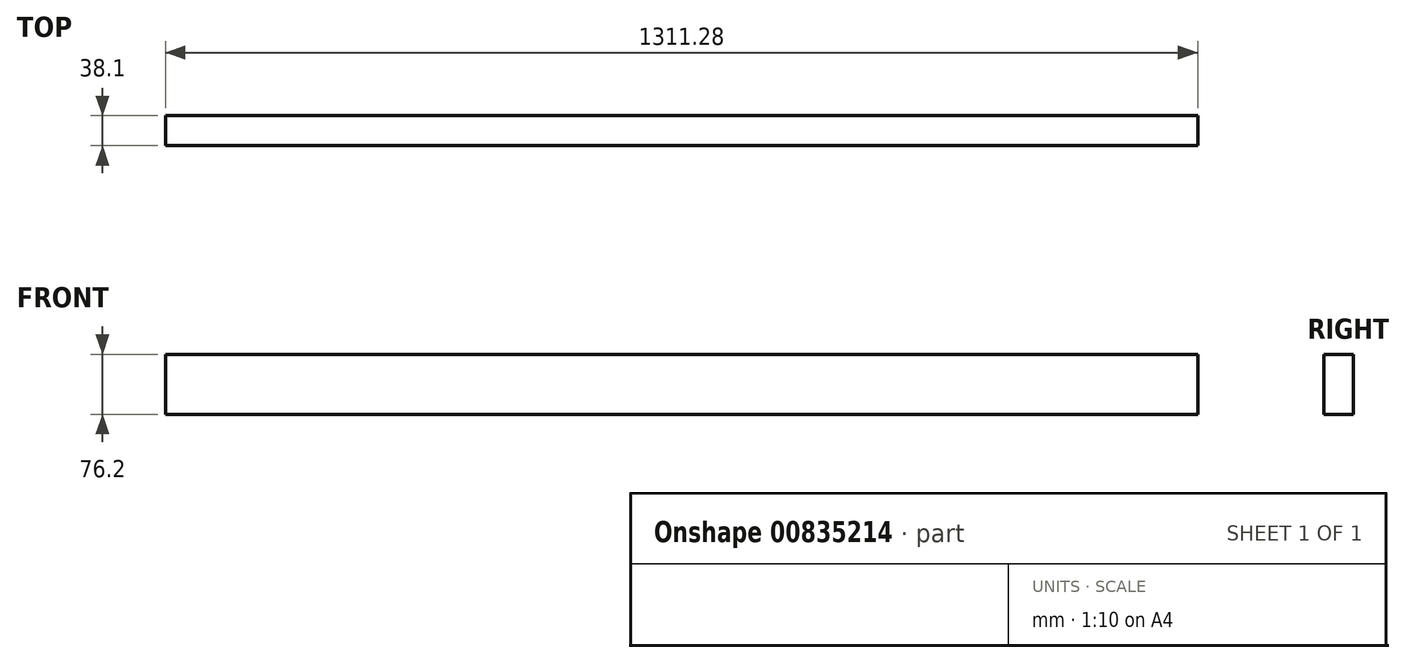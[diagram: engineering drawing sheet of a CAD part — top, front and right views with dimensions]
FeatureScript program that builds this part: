
annotation { "Feature Type Name" : "Feature", "Feature Type Description" : "" }
export const myFeature = defineFeature(function(context is Context, id is Id, definition is map)
    precondition{}
    {
        {
            var Q0;
            Q0=qCreatedBy(makeId("Right.planeOp"),FACE);
            var sketch = newSketch(context, id + "F0", { "sketchPlane" : qUnion([Q0])});
            skLineSegment(sketch, "E0.bottom", {"start": v(19.05, 38.1) * mm, "end": v(-19.05, 38.1) * mm});
            skLineSegment(sketch, "E0.top", {"start": v(19.05, -38.1) * mm, "end": v(-19.05, -38.1) * mm});
            skLineSegment(sketch, "E0.left", {"start": v(19.05, 38.1) * mm, "end": v(19.05, -38.1) * mm});
            skLineSegment(sketch, "E0.right", {"start": v(-19.05, 38.1) * mm, "end": v(-19.05, -38.1) * mm});
            skPoint(sketch, "E0.middle", {"position": v(0, 0) * mm});
            skSolve(sketch);
        }
        {
            var Q0;
            Q0 = qSketchRegion(id + "F0", true);
            extrude(context, id + "F1", {"entities" : qUnion([Q0]), "endBound" : BoundingType.SYMMETRIC, "depth" : 1311.27 * mm, "offsetDistance" : 25.4 * mm});
        }
    });
